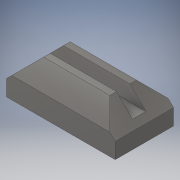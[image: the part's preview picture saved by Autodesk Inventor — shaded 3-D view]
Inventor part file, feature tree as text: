
AUTODESK INVENTOR PART (.ipt)
format: ipt  version: 2019 (Build 230136000, 136)  size: 121,856 bytes
history: native  units: in
note: dims shown in document units (in); Inventor stores cm internally (conversion verified against a paired STEP export)
features: extrude x2, chamfer x2, sketch x2
ambient origin geometry x8: Origin, YZ Plane, XZ Plane, XY Plane, X Axis, Y Axis, Z Axis, Center Point
bodies: Solid1 (feature_tree)
feature tree (6):
  extrude  "Extrusion1"  Depth=2.75in
  extrude  "Extrusion2"  Depth=0.75in
  chamfer  "Chamfer1"  Distance=0.625in
  chamfer  "Chamfer2"  Distance=0.75in
  sketch  "Sketch1"  dims[d0=5.125in d1=2.75in]
  sketch  "Sketch2"  dims[d2=1.75in d3=0.0in d4=0.3125in d5=0.625in d6=0.75in d7=0.0in d8=1.0in d9=0.125in d10=45.0deg d11=0.75in d12=0.125in d13=45.0deg]
